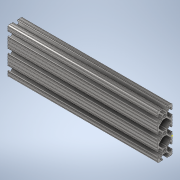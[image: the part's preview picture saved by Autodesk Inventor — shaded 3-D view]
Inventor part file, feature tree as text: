
AUTODESK INVENTOR PART (.ipt)
format: ipt  version: 2020 (Build 240168000, 168)  size: 376,320 bytes
history: native  units: in
note: dims shown in document units (in); Inventor stores cm internally (conversion verified against a paired STEP export)
features: sketch x2, extrude x1
ambient origin geometry x8: Origin, YZ Plane, XZ Plane, XY Plane, X Axis, Y Axis, Z Axis, Center Point
bodies: Solid1 (feature_tree)
feature tree (3):
  extrude  "Extrusion1"  [1 undecoded]
  sketch  "Sketch2"
  sketch  "Sketch1"  dims[d0=10.0in d1=0.0in]
note: 1 required parameter value undecoded (feature->parameter linkage not recoverable at this tier; creation-order binding heuristic only, values carry confidence <= 0.55)
